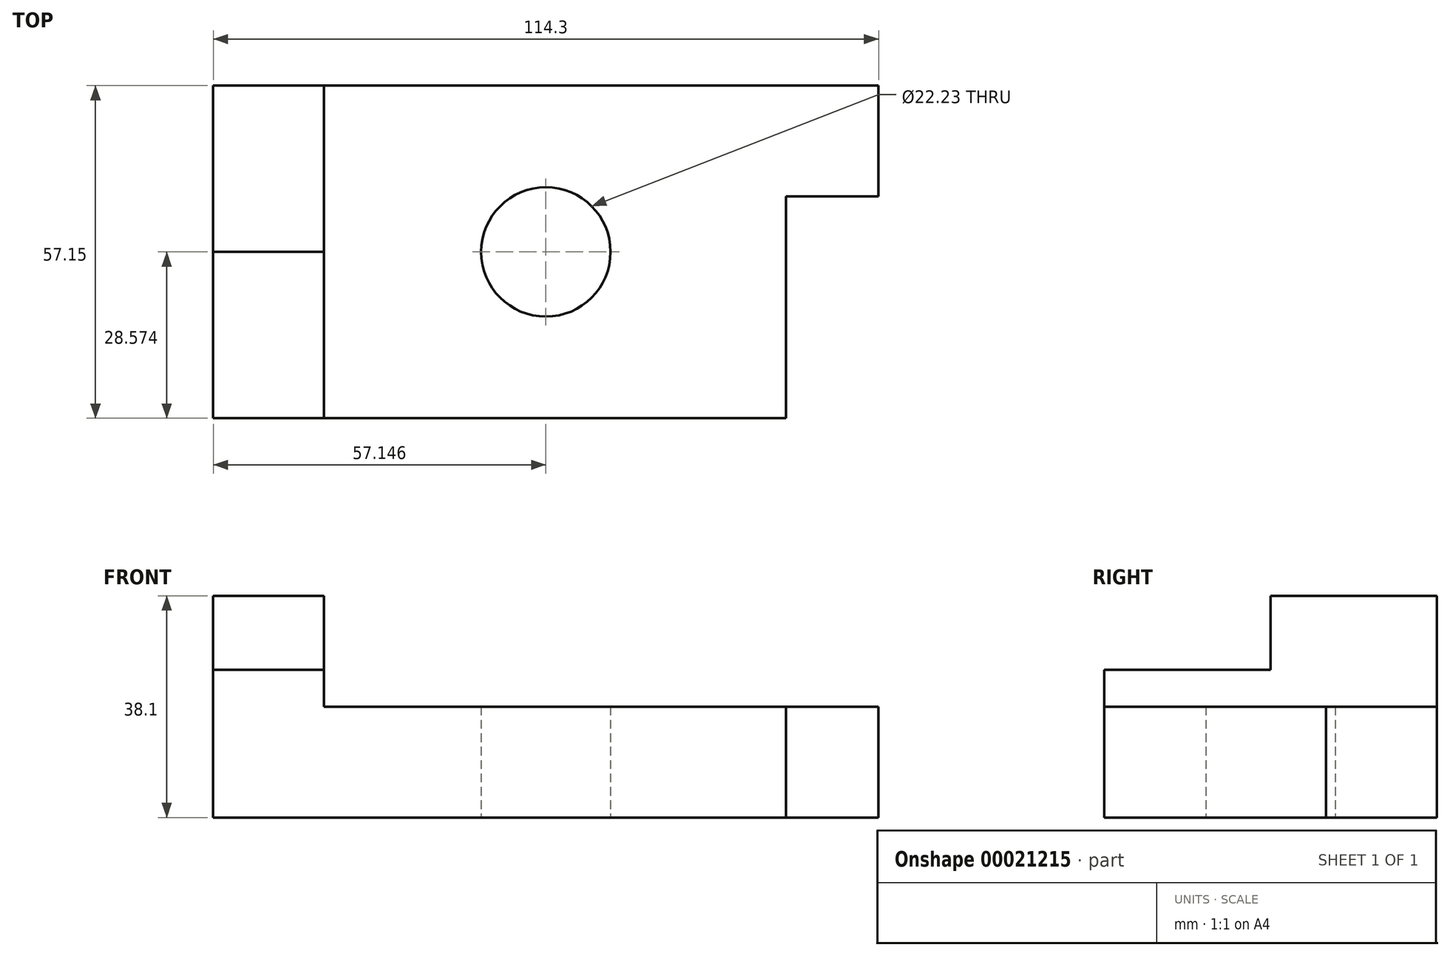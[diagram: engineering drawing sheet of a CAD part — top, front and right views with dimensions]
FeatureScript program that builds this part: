
annotation { "Feature Type Name" : "Feature", "Feature Type Description" : "" }
export const myFeature = defineFeature(function(context is Context, id is Id, definition is map)
    precondition{}
    {
        {
            var Q0;
            Q0=qCreatedBy(makeId("Top.planeOp"),FACE);
            var sketch = newSketch(context, id + "F0", { "sketchPlane" : qUnion([Q0])});
            skLineSegment(sketch, "E0.bottom", {"start": v(-55.51, 37.24) * mm, "end": v(-36.46, 37.24) * mm});
            skLineSegment(sketch, "E0.top", {"start": v(-55.51, 8.66) * mm, "end": v(-36.46, 8.66) * mm});
            skLineSegment(sketch, "E0.left", {"start": v(-55.51, 37.24) * mm, "end": v(-55.51, 8.66) * mm});
            skLineSegment(sketch, "E0.right", {"start": v(-36.46, 37.24) * mm, "end": v(-36.46, 8.66) * mm});
            skLineSegment(sketch, "E1.top", {"start": v(-55.51, -19.91) * mm, "end": v(-36.46, -19.91) * mm});
            skLineSegment(sketch, "E1.left", {"start": v(-55.51, 8.66) * mm, "end": v(-55.51, -19.91) * mm});
            skLineSegment(sketch, "E1.right", {"start": v(-36.46, 8.66) * mm, "end": v(-36.46, -19.91) * mm});
            skLineSegment(sketch, "E2.bottom", {"start": v(-55.51, 37.24) * mm, "end": v(58.79, 37.24) * mm});
            skLineSegment(sketch, "E2.top", {"start": v(-55.51, -19.91) * mm, "end": v(42.91, -19.91) * mm});
            skLineSegment(sketch, "E2.left", {"start": v(-55.51, 37.24) * mm, "end": v(-55.51, -19.91) * mm});
            skLineSegment(sketch, "E2.right", {"start": v(58.79, 37.24) * mm, "end": v(58.79, 18.19) * mm});
            skLineSegment(sketch, "E3.top", {"start": v(58.79, 18.19) * mm, "end": v(42.91, 18.19) * mm});
            skLineSegment(sketch, "E3.right", {"start": v(42.91, -19.91) * mm, "end": v(42.91, 18.19) * mm});
            skPoint(sketch, "E4.orphan", {"position": v(58.79, -19.91) * mm});
            skLineSegment(sketch, "E5", {"start": v(58.79, 37.24) * mm, "end": v(0, 37.24) * mm});
            skCircle(sketch, "E6", {"center": v(1.64, 8.66) * mm, "radius": 11.11 * mm});
            skPoint(sketch, "E7.end.orphan", {"position": v(-19.56, 8.66) * mm});
            skPoint(sketch, "E8.start.orphan", {"position": v(58.79, 5.92) * mm});
            skPoint(sketch, "E9.trimOffspring.end.orphan", {"position": v(1.64, 5.92) * mm});
            skSolve(sketch);
        }
        {
            var Q0;
            {var subQ5=sQuery(id+"F0.wireOp",EDGE,"E0.right");Q0=makeQuery(id+"F0.imprint","IMPRINT",FACE,{"disambiguationData":[TD([[makeQuery(id+"F0.imprint","IMPRINT",EDGE,{"derivedFrom":subQ5}),1.0]])]});}
            extrude(context, id + "F1", {"entities" : qUnion([Q0]), "depth" : 19.05 * mm});
        }
        {
            var Q0;
            {var subQ3=sQuery(id+"F0.wireOp",EDGE,"E0.right");Q0=makeQuery(id+"F0.imprint","IMPRINT",FACE,{"disambiguationData":[TD([[makeQuery(id+"F0.imprint","IMPRINT",EDGE,{"derivedFrom":subQ3}),-1.0]])]});}
            extrude(context, id + "F2", {"entities" : qUnion([Q0]), "operationType" : NewBodyOperationType.ADD, "depth" : 38.1 * mm});
        }
        {
            var Q0;
            {var subQ3=sQuery(id+"F0.wireOp",EDGE,"E0.top");Q0=makeQuery(id+"F0.imprint","IMPRINT",FACE,{"disambiguationData":[TD([[makeQuery(id+"F0.imprint","IMPRINT",EDGE,{"derivedFrom":subQ3}),-1.0]])]});}
            extrude(context, id + "F3", {"entities" : qUnion([Q0]), "operationType" : NewBodyOperationType.ADD, "depth" : 25.4 * mm});
        }
    });
